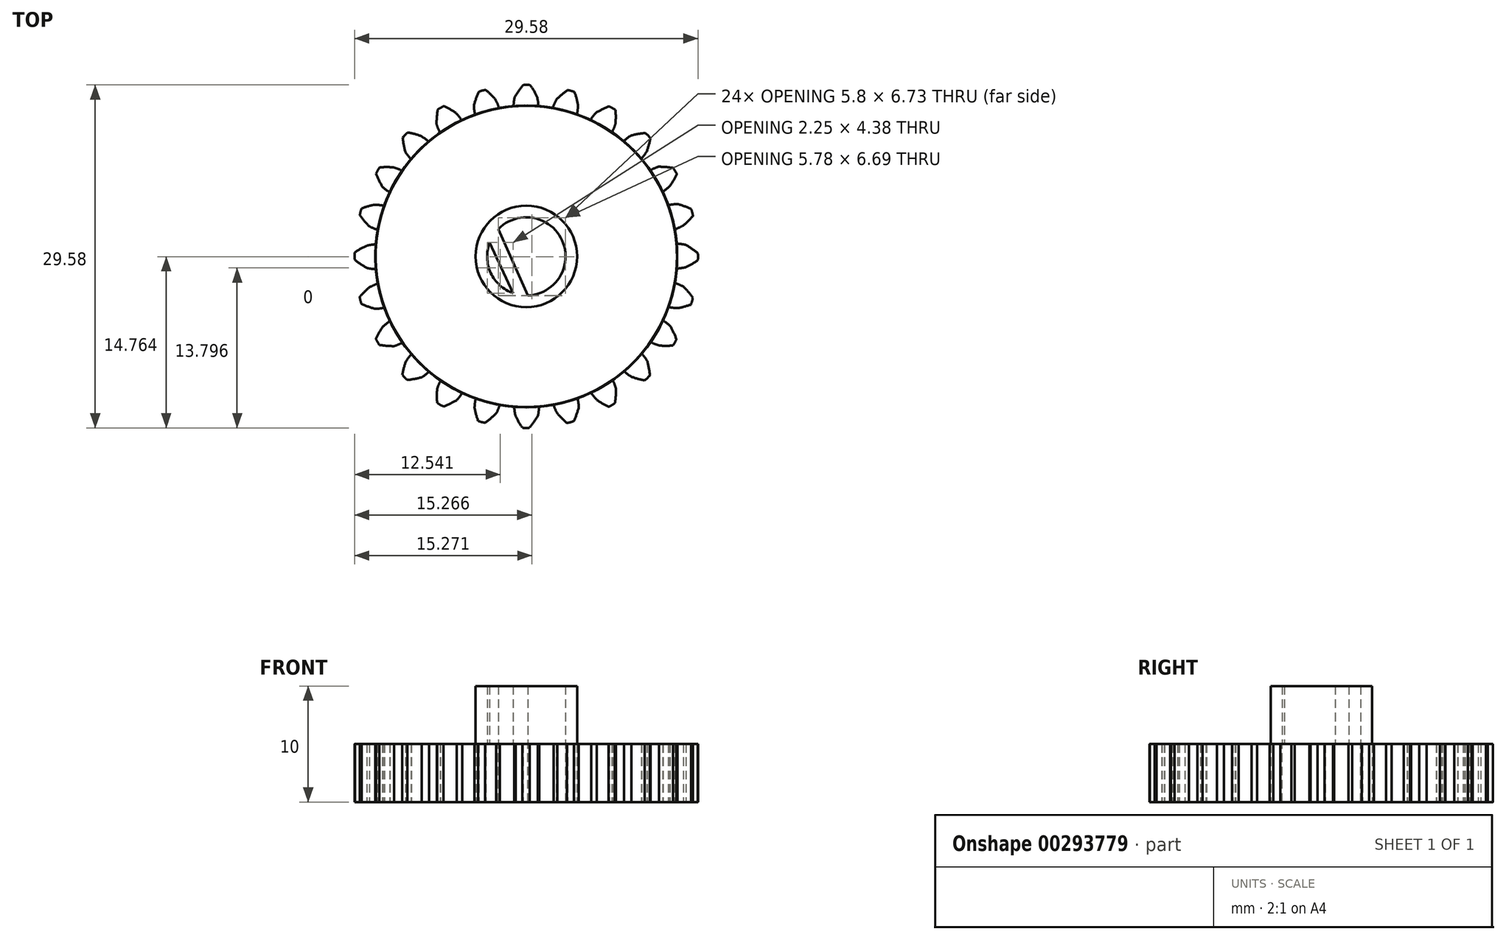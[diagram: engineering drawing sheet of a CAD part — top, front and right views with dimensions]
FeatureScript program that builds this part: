
annotation { "Feature Type Name" : "Feature", "Feature Type Description" : "" }
export const myFeature = defineFeature(function(context is Context, id is Id, definition is map)
    precondition{}
    {
        {
            var Q0;
            Q0=qCreatedBy(makeId("Top.planeOp"),FACE);
            var sketch = newSketch(context, id + "F0", { "sketchPlane" : qUnion([Q0])});
            skCircle(sketch, "E0", {"center": v(0, 0) * mm, "radius": 15 * mm, "construction": true});
            skCircle(sketch, "E1", {"center": v(0, 0.27) * mm, "radius": 13 * mm});
            skCircle(sketch, "E2", {"center": v(0, 0) * mm, "radius": 16 * mm, "construction": true});
            skLineSegment(sketch, "E3", {"start": v(0, 0) * mm, "end": v(0, 16) * mm, "construction": true});
            skLineSegment(sketch, "E4", {"start": v(0, 13) * mm, "end": v(-1, 13) * mm, "construction": true});
            skLineSegment(sketch, "E5", {"start": v(0, 13) * mm, "end": v(1, 13) * mm, "construction": true});
            skArc(sketch, "E6", {"start": v(0.39, 13) * mm, "mid": v(0.25, 13) * mm, "end": v(0.12, 13) * mm});
            skArc(sketch, "E7", {"start": v(0, 5.06) * mm, "mid": v(0, 5.07) * mm, "end": v(0, 5.07) * mm});
            skArc(sketch, "E8.trimOffspring", {"start": v(-0.12, 13) * mm, "mid": v(-0.25, 13) * mm, "end": v(-0.38, 13) * mm});
            skLineSegment(sketch, "E9.trimOffspring", {"start": v(0, 5.07) * mm, "end": v(0, 117.25) * mm, "construction": true});
            skPoint(sketch, "E10.start.orphan", {"position": v(1.02, 3.76) * mm});
            skPoint(sketch, "E11.start.orphan", {"position": v(1.02, 3.84) * mm});
            skArc(sketch, "E12", {"start": v(0.95, 14.97) * mm, "mid": v(0.94, 14.99) * mm, "end": v(0.94, 15) * mm});
            skArc(sketch, "E13.trimOffspring", {"start": v(-1, 15) * mm, "mid": v(-1, 14.99) * mm, "end": v(-1, 14.97) * mm});
            skArc(sketch, "E14.trimOffspring", {"start": v(-1.1, 13.95) * mm, "mid": v(-1.1, 13.95) * mm, "end": v(-1.1, 13.95) * mm});
            skArc(sketch, "E15", {"start": v(1.05, 12.96) * mm, "mid": v(1.03, 13.49) * mm, "end": v(0.94, 14.01) * mm});
            skArc(sketch, "E16.trimOffspring", {"start": v(-0.99, 14.01) * mm, "mid": v(-1.07, 13.49) * mm, "end": v(-1.1, 12.96) * mm});
            skArc(sketch, "E17", {"start": v(0.94, 14.01) * mm, "mid": v(0.67, 14.54) * mm, "end": v(0.35, 15.04) * mm});
            skArc(sketch, "E18", {"start": v(0.35, 15.04) * mm, "mid": v(0.03, 15.06) * mm, "end": v(-0.28, 15.04) * mm});
            skArc(sketch, "E19.trimOffspring", {"start": v(-0.28, 15.04) * mm, "mid": v(-0.65, 14.54) * mm, "end": v(-0.99, 14.01) * mm});
            skSolve(sketch);
        }
        {
            var Q0;
            Q0=qSketchRegion(id+"F0",true);
            extrude(context, id + "F1", {"entities" : qUnion([Q0]), "depth" : 5 * mm});
        }
        {
            var Q0;
            Q0=makeQuery(id+"F1.opExtrude","SWEPT_BODY",BODY,{"disambiguationData":[OSD([sQuery(id+"F0.wireOp",EDGE,"E1"),sQuery(id+"F0.wireOp",EDGE,"E6"),sQuery(id+"F0.wireOp",EDGE,"8135d3ed-eb66-4b9b-a605-aa948f9b6877.trimOffspring"),sQuery(id+"F0.wireOp",EDGE,"E7"),sQuery(id+"F0.wireOp",EDGE,"NEc80oSd-jkKK-Rj08-4cXk-I9QzhTEvkPhy"),sQuery(id+"F0.wireOp",EDGE,"69d1582d-723c-4c18-846d-3caa5e789cbb.trimOffspring")])]});
            var Q1;
            Q1=makeQuery(id+"F1.opExtrude","SWEPT_FACE",FACE,{"disambiguationData":[OSD([sQuery(id+"F0.wireOp",EDGE,"E1")])]});
            circularPattern(context, id + "F2", {"entities" : qUnion([Q0]), "axis" : qUnion([Q1]), "angle" : 360 * degree, "instanceCount" : 24, "equalSpace" : true});
        }
        {
            var Q0;
            Q0=makeQuery(id+"F1.opExtrude","CAP_FACE",FACE,{"disambiguationData":[OSD([sQuery(id+"F0.wireOp",EDGE,"E1"),sQuery(id+"F0.wireOp",EDGE,"E6"),sQuery(id+"F0.wireOp",EDGE,"8135d3ed-eb66-4b9b-a605-aa948f9b6877.trimOffspring"),sQuery(id+"F0.wireOp",EDGE,"E7"),sQuery(id+"F0.wireOp",EDGE,"NEc80oSd-jkKK-Rj08-4cXk-I9QzhTEvkPhy"),sQuery(id+"F0.wireOp",EDGE,"69d1582d-723c-4c18-846d-3caa5e789cbb.trimOffspring")])],"isStart":false});
            var sketch = newSketch(context, id + "F3", { "sketchPlane" : qUnion([Q0])});
            skPoint(sketch, "E20.middle", {"position": v(0, 0) * mm});
            skPoint(sketch, "E20.right.end.orphan", {"position": v(-2.12, 2.12) * mm});
            skPoint(sketch, "E21.right.end.orphan", {"position": v(-3.33, 3.33) * mm});
            skPoint(sketch, "E20.bottom.end.orphan", {"position": v(-2.12, -2.12) * mm});
            skPoint(sketch, "E20.left.end.orphan", {"position": v(2.12, 2.12) * mm});
            skPoint(sketch, "E20.left.start.orphan", {"position": v(2.12, -2.12) * mm});
            skPoint(sketch, "E21.left.end.orphan", {"position": v(3.33, 3.33) * mm});
            skPoint(sketch, "E21.bottom.end.orphan", {"position": v(-3.33, -3.33) * mm});
            skPoint(sketch, "E21.bottom.start.orphan", {"position": v(3.33, -3.33) * mm});
            skArc(sketch, "E22", {"start": v(-3.37, 0.06) * mm, "mid": v(-3.37, 0.03) * mm, "end": v(-3.38, 0) * mm});
            skLineSegment(sketch, "E23", {"start": v(0, 3.62) * mm, "end": v(0, 3.66) * mm});
            skLineSegment(sketch, "E24", {"start": v(0, 0) * mm, "end": v(0, 0.25) * mm});
            skCircle(sketch, "E25", {"center": v(0, 0.27) * mm, "radius": 3.4 * mm});
            skPoint(sketch, "E26.orphan", {"position": v(0, 13.22) * mm});
            skLineSegment(sketch, "E27", {"start": v(-2.41, 2.64) * mm, "end": v(0.13, -3.12) * mm});
            skPoint(sketch, "E28.start.orphan", {"position": v(0, -3.12) * mm});
            skPoint(sketch, "E29.orphan", {"position": v(3.38, 0) * mm});
            skLineSegment(sketch, "E30", {"start": v(0, 3.66) * mm, "end": v(0, 13.22) * mm});
            skLineSegment(sketch, "E31", {"start": v(0.13, -3.12) * mm, "end": v(0.13, -12.73) * mm});
            skSolve(sketch);
        }
        {
            var Q0;
            {var subQ0=sQuery(id+"F3.wireOp",EDGE,"E28");Q0=makeQuery(id+"F3.imprint","IMPRINT",FACE,{"disambiguationData":[TD([[makeQuery(id+"F3.imprint","IMPRINT",EDGE,{"derivedFrom":subQ0}),-1.0]])]});}
            var Q1;
            {var subQ2=sQuery(id+"F3.wireOp",EDGE,"E27");Q1=makeQuery(id+"F3.imprint","IMPRINT",FACE,{"disambiguationData":[TD([[makeQuery(id+"F3.imprint","IMPRINT",EDGE,{"derivedFrom":subQ2}),1.0]])]});}
            extrude(context, id + "F4", {"entities" : qUnion([Q0, Q1]), "operationType" : NewBodyOperationType.REMOVE, "oppositeDirection" : true, "depth" : 25 * mm});
        }
        {
            var Q0;
            Q0=makeQuery(id+"F2.opPattern","COPY",FACE,{"derivedFrom":makeQuery(id+"F1.opExtrude","CAP_FACE",FACE,{"disambiguationData":[OSD([sQuery(id+"F0.wireOp",EDGE,"E1"),sQuery(id+"F0.wireOp",EDGE,"ce9dac7b-c6a7-4aa2-8854-a52381f8a8e8"),sQuery(id+"F0.wireOp",EDGE,"06ce8aa9-c749-40ed-9192-5f1dd213df4d.trimOffspring"),sQuery(id+"F0.wireOp",EDGE,"f63a663b-90d1-4972-b024-fb19c3c43451"),sQuery(id+"F0.wireOp",EDGE,"90c57f24-a5db-4b47-97ce-a6af5debadce"),sQuery(id+"F0.wireOp",EDGE,"e15c1dc4-cf10-48a9-8e95-0bd51a33337e.trimOffspring")])],"isStart":false}),"instanceName":"9"});
            var sketch = newSketch(context, id + "F5", { "sketchPlane" : qUnion([Q0])});
            skPoint(sketch, "E32.start.orphan", {"position": v(-2.22, 2.54) * mm});
            skPoint(sketch, "E33.start.orphan", {"position": v(-3.25, 2.54) * mm});
            skCircle(sketch, "E34", {"center": v(0, 0.27) * mm, "radius": 3.38 * mm});
            skCircle(sketch, "E35", {"center": v(0, 0.27) * mm, "radius": 4.38 * mm});
            skLineSegment(sketch, "E36", {"start": v(-0.58, -4.07) * mm, "end": v(-3.68, 2.62) * mm});
            skSolve(sketch);
        }
        {
            var Q0;
            Q0 = qSketchRegion(id + "F5", true);
            var Q1;
            {var subQ0=sQuery(id+"F5.wireOp",EDGE,"E33");var subQ1=sQuery(id+"F5.wireOp",EDGE,"pEozFyju-i5PG-pIGt-Xkxd-JWm3oXukfSJh");var subQ2=makeQuery(id+"F5.imprint","INTERSECT",VERTEX,{"disambiguationData":[OD(0.0)],"derivedFrom":[subQ1,subQ0]});Q1=makeQuery(id+"F5.imprint","IMPRINT",FACE,{"disambiguationData":[TD([[makeQuery(id+"F5.imprint","IMPRINT",EDGE,{"disambiguationData":[TD([[subQ2,-1.0]])],"derivedFrom":subQ1}),1.0]])]});}
            var Q2;
            {var subQ0=sQuery(id+"F5.wireOp",EDGE,"E32");Q2=makeQuery(id+"F5.imprint","IMPRINT",FACE,{"disambiguationData":[TD([[makeQuery(id+"F5.imprint","IMPRINT",EDGE,{"derivedFrom":subQ0}),1.0]])]});}
            var Q3;
            {var subQ0=sQuery(id+"F5.wireOp",EDGE,"E36");var subQ1=sQuery(id+"F5.wireOp",EDGE,"E34");var subQ2=makeQuery(id+"F5.imprint","INTERSECT",VERTEX,{"disambiguationData":[OD(0.0)],"derivedFrom":[subQ1,subQ0]});Q3=makeQuery(id+"F5.imprint","IMPRINT",FACE,{"disambiguationData":[TD([[makeQuery(id+"F5.imprint","IMPRINT",EDGE,{"disambiguationData":[TD([[subQ2,1.0]])],"derivedFrom":subQ0}),-1.0]])]});}
            var Q4;
            {var subQ0=sQuery(id+"F5.wireOp",EDGE,"E36");var subQ1=sQuery(id+"F5.wireOp",EDGE,"E34");var subQ2=makeQuery(id+"F5.imprint","INTERSECT",VERTEX,{"disambiguationData":[OD(0.0)],"derivedFrom":[subQ1,subQ0]});Q4=makeQuery(id+"F5.imprint","IMPRINT",FACE,{"disambiguationData":[TD([[makeQuery(id+"F5.imprint","IMPRINT",EDGE,{"disambiguationData":[TD([[subQ2,-1.0]])],"derivedFrom":subQ1}),1.0]])]});}
            extrude(context, id + "F6", {"entities" : qUnion([Q0, Q1, Q2, Q3, Q4]), "depth" : 5 * mm});
        }
    });
